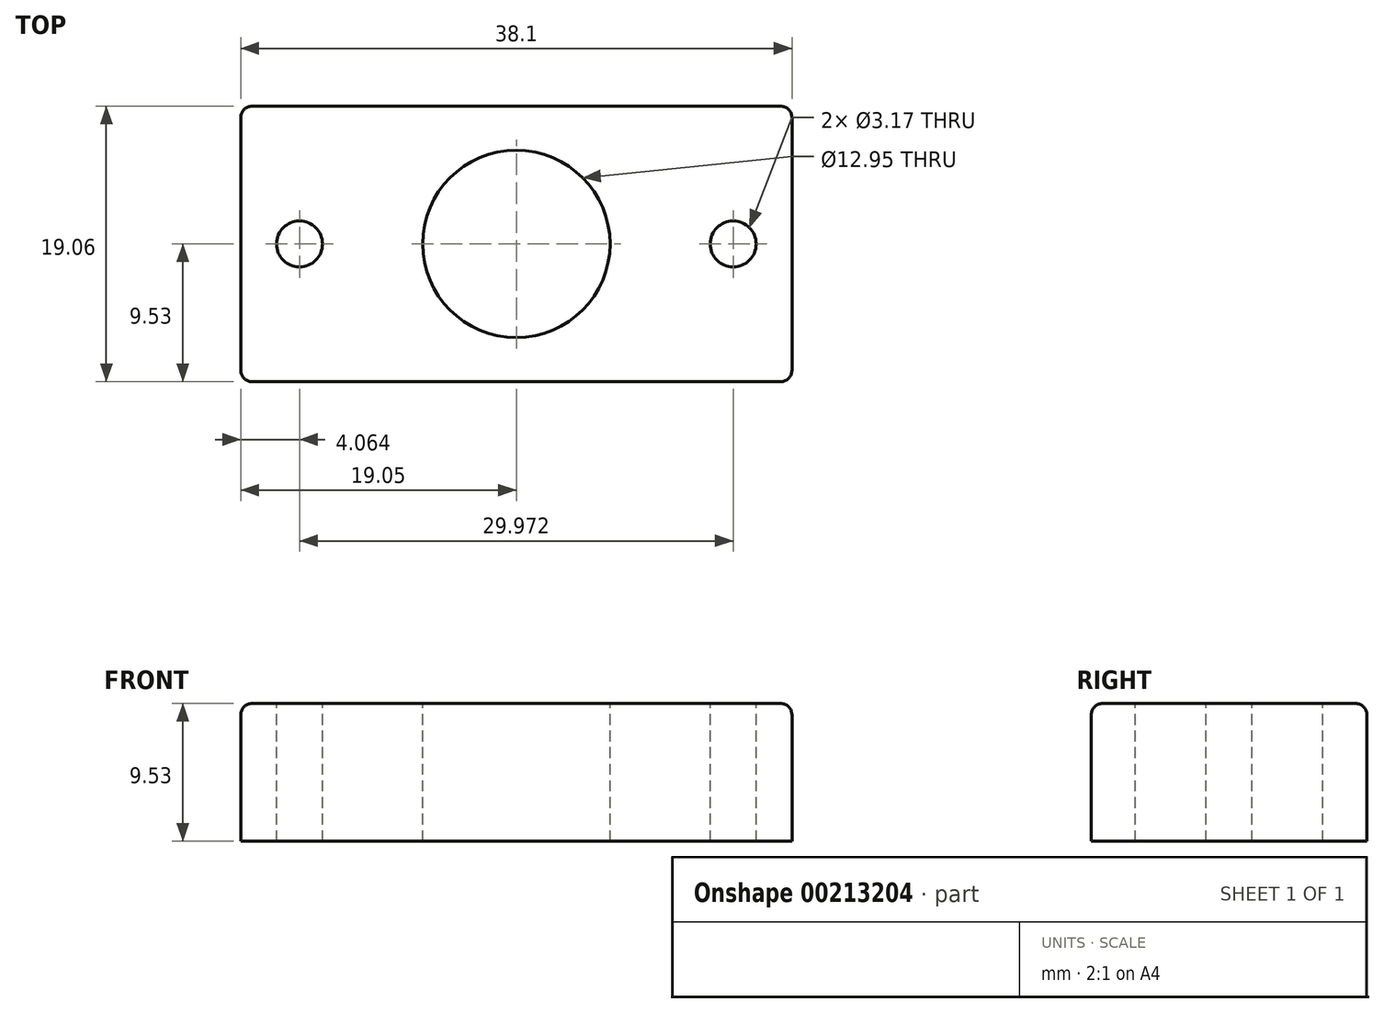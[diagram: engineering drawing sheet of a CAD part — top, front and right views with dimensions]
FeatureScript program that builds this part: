
annotation { "Feature Type Name" : "Feature", "Feature Type Description" : "" }
export const myFeature = defineFeature(function(context is Context, id is Id, definition is map)
    precondition{}
    {
        {
            var Q0;
            Q0=qCreatedBy(makeId("Top.planeOp"),FACE);
            var sketch = newSketch(context, id + "F0", { "sketchPlane" : qUnion([Q0])});
            skLineSegment(sketch, "E0.bottom", {"start": v(19.05, 9.53) * mm, "end": v(-19.05, 9.53) * mm});
            skLineSegment(sketch, "E0.top", {"start": v(19.05, -9.53) * mm, "end": v(-19.05, -9.53) * mm});
            skLineSegment(sketch, "E0.left", {"start": v(19.05, 9.53) * mm, "end": v(19.05, -9.53) * mm});
            skLineSegment(sketch, "E0.right", {"start": v(-19.05, 9.53) * mm, "end": v(-19.05, -9.53) * mm});
            skPoint(sketch, "E0.middle", {"position": v(0, 0) * mm});
            skSolve(sketch);
        }
        {
            var Q0;
            Q0 = qSketchRegion(id + "F0", true);
            extrude(context, id + "F1", {"entities" : qUnion([Q0]), "depth" : 9.52 * mm});
        }
        {
            var Q0;
            Q0=makeQuery(id+"F1.opExtrude","CAP_FACE",FACE,{"disambiguationData":[OSD([sQuery(id+"F0.wireOp",EDGE,"E0.bottom"),sQuery(id+"F0.wireOp",EDGE,"E0.top"),sQuery(id+"F0.wireOp",EDGE,"E0.left"),sQuery(id+"F0.wireOp",EDGE,"E0.right")])],"isStart":false});
            var sketch = newSketch(context, id + "F2", { "sketchPlane" : qUnion([Q0])});
            skCircle(sketch, "E1", {"center": v(-14.99, 0) * mm, "radius": 1.59 * mm});
            skCircle(sketch, "E2", {"center": v(14.99, 0) * mm, "radius": 1.59 * mm});
            skPoint(sketch, "E3", {"position": v(0, 0) * mm});
            skSolve(sketch);
        }
        {
            var Q0;
            Q0 = qSketchRegion(id + "F2", true);
            extrude(context, id + "F3", {"entities" : qUnion([Q0]), "operationType" : NewBodyOperationType.REMOVE, "endBound" : BoundingType.UP_TO_NEXT, "oppositeDirection" : true, "depth" : 25.4 * mm});
        }
        {
            var Q0;
            Q0=makeQuery(id+"F1.opExtrude","CAP_EDGE",EDGE,{"disambiguationData":[OSD([sQuery(id+"F0.wireOp",EDGE,"E0.top")])],"isStart":false});
            var Q1;
            Q1=makeQuery(id+"F1.opExtrude","CAP_EDGE",EDGE,{"disambiguationData":[OSD([sQuery(id+"F0.wireOp",EDGE,"E0.right")])],"isStart":false});
            var Q2;
            Q2=makeQuery(id+"F1.opExtrude","CAP_EDGE",EDGE,{"disambiguationData":[OSD([sQuery(id+"F0.wireOp",EDGE,"E0.bottom")])],"isStart":false});
            var Q3;
            Q3=makeQuery(id+"F1.opExtrude","CAP_EDGE",EDGE,{"disambiguationData":[OSD([sQuery(id+"F0.wireOp",EDGE,"E0.left")])],"isStart":false});
            var Q4;
            Q4=makeQuery(id+"F1.opExtrude","SWEPT_EDGE",EDGE,{"disambiguationData":[OSD([sQuery(id+"F0.wireOp",EDGE,"E0.top"),sQuery(id+"F0.wireOp",EDGE,"E0.left")])]});
            var Q5;
            Q5=makeQuery(id+"F1.opExtrude","SWEPT_EDGE",EDGE,{"disambiguationData":[OSD([sQuery(id+"F0.wireOp",EDGE,"E0.bottom"),sQuery(id+"F0.wireOp",EDGE,"E0.left")])]});
            var Q6;
            Q6=makeQuery(id+"F1.opExtrude","SWEPT_EDGE",EDGE,{"disambiguationData":[OSD([sQuery(id+"F0.wireOp",EDGE,"E0.top"),sQuery(id+"F0.wireOp",EDGE,"E0.right")])]});
            var Q7;
            Q7=makeQuery(id+"F1.opExtrude","SWEPT_EDGE",EDGE,{"disambiguationData":[OSD([sQuery(id+"F0.wireOp",EDGE,"E0.bottom"),sQuery(id+"F0.wireOp",EDGE,"E0.right")])]});
            fillet(context, id + "F4", {"entities" : qUnion([Q0, Q1, Q2, Q3, Q4, Q5, Q6, Q7]), "radius" : 0.79 * mm, "tangentPropagation" : true, "allowEdgeOverflow" : false});
        }
        {
            var Q0;
            Q0=sQuery(id+"F2.wireOp",VERTEX,"E3");
            var Q1;
            Q1=makeQuery(id+"F1.opExtrude","SWEPT_BODY",BODY,{"disambiguationData":[OSD([sQuery(id+"F0.wireOp",EDGE,"E0.bottom"),sQuery(id+"F0.wireOp",EDGE,"E0.top"),sQuery(id+"F0.wireOp",EDGE,"E0.left"),sQuery(id+"F0.wireOp",EDGE,"E0.right")])]});
            hole(context, id + "F5", {"style" : HoleStyle.SIMPLE, "endStyle" : HoleEndStyle.THROUGH, "holeDiameter" : 12.95 * mm, "tappedDepth" : 12.7 * mm, "tapClearance" : 3, "locations" : qUnion([Q0]), "scope" : qUnion([Q1])});
        }
    });
